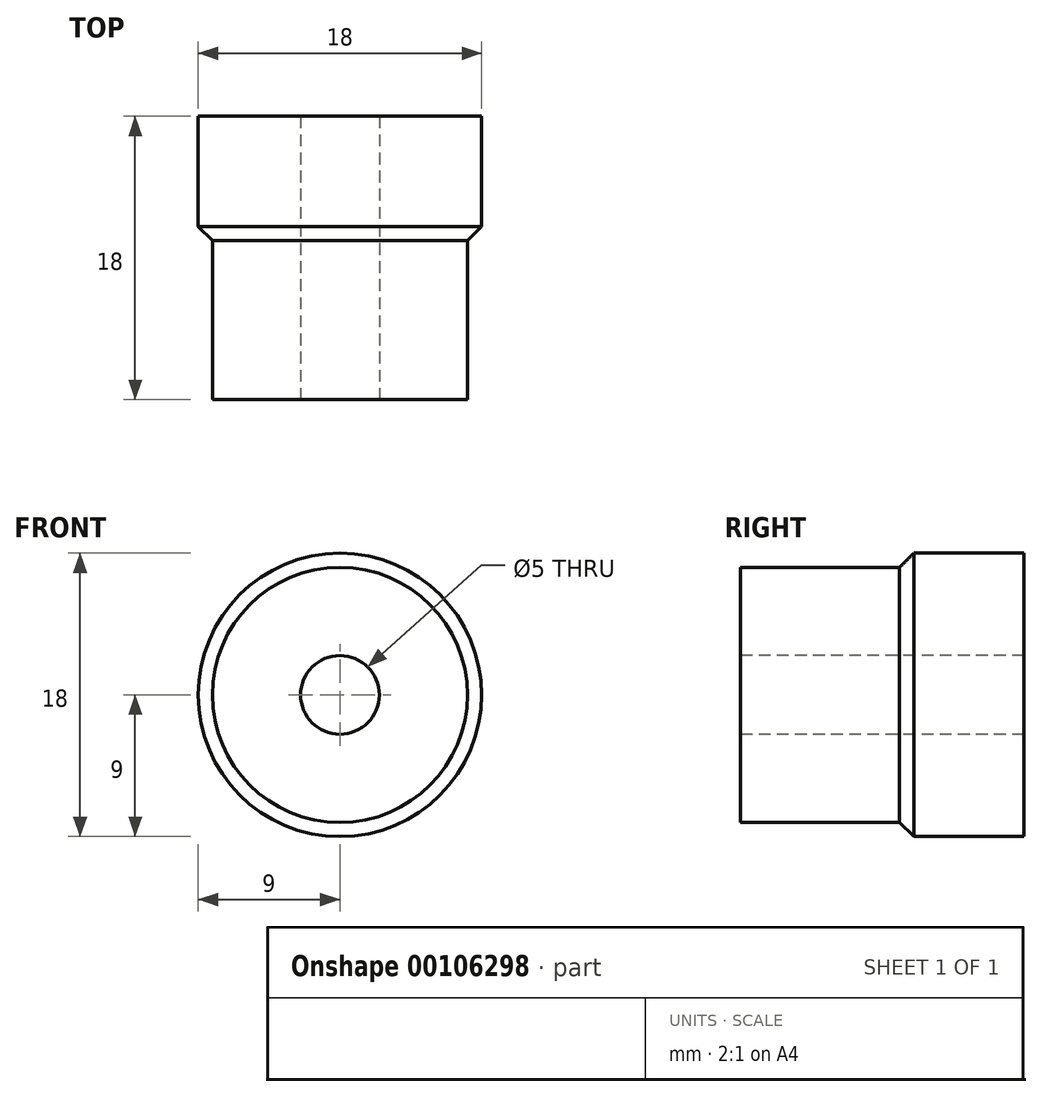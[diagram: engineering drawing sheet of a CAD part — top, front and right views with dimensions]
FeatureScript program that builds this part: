
annotation { "Feature Type Name" : "Feature", "Feature Type Description" : "" }
export const myFeature = defineFeature(function(context is Context, id is Id, definition is map)
    precondition{}
    {
        {
            var Q0;
            Q0=qCreatedBy(makeId("Front.planeOp"),FACE);
            var sketch = newSketch(context, id + "F0", { "sketchPlane" : qUnion([Q0])});
            skCircle(sketch, "E0", {"center": v(0, 0) * mm, "radius": 9 * mm});
            skSolve(sketch);
        }
        {
            var Q0;
            Q0=qSketchRegion(id+"F0",true);
            extrude(context, id + "F1", {"entities" : qUnion([Q0]), "depth" : 8 * mm});
        }
        {
            var Q0;
            Q0=makeQuery(id+"F1.opExtrude","CAP_FACE",FACE,{"disambiguationData":[OSD([sQuery(id+"F0.wireOp",EDGE,"E0")])],"isStart":false});
            var sketch = newSketch(context, id + "F2", { "sketchPlane" : qUnion([Q0])});
            skCircle(sketch, "E1", {"center": v(0, 0) * mm, "radius": 8.1 * mm});
            skSolve(sketch);
        }
        {
            var Q0;
            Q0=qSketchRegion(id+"F2",true);
            extrude(context, id + "F3", {"entities" : qUnion([Q0]), "operationType" : NewBodyOperationType.ADD, "depth" : 10 * mm});
        }
        {
            var Q0;
            Q0=makeQuery(id+"F1.opExtrude","CAP_EDGE",EDGE,{"disambiguationData":[OSD([sQuery(id+"F0.wireOp",EDGE,"E0")])],"isStart":false});
            chamfer(context, id + "F4", {"entities" : qUnion([Q0]), "width" : 1 * mm, "tangentPropagation" : true});
        }
        {
            var Q0;
            Q0=makeQuery(id+"F3.opExtrude","CAP_FACE",FACE,{"disambiguationData":[OSD([sQuery(id+"F2.wireOp",EDGE,"E1")])],"isStart":false});
            var sketch = newSketch(context, id + "F5", { "sketchPlane" : qUnion([Q0])});
            skCircle(sketch, "E2", {"center": v(0, 0) * mm, "radius": 2.5 * mm});
            skSolve(sketch);
        }
        {
            var Q0;
            Q0=qSketchRegion(id+"F5",true);
            extrude(context, id + "F6", {"entities" : qUnion([Q0]), "operationType" : NewBodyOperationType.REMOVE, "endBound" : BoundingType.THROUGH_ALL, "oppositeDirection" : true, "depth" : 25 * mm});
        }
    });
